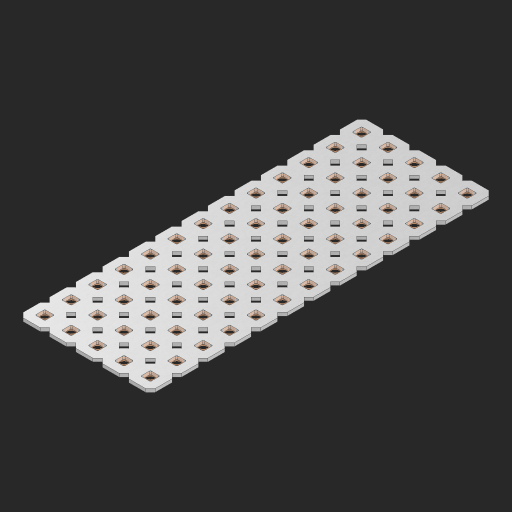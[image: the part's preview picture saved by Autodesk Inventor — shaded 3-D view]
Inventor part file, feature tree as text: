
AUTODESK INVENTOR PART (.ipt)
format: ipt  version: 2023 (Build 270158000, 158)  size: 1,042,432 bytes
history: native  units: in
note: dims shown in document units (in); Inventor stores cm internally (conversion verified against a paired STEP export)
features: other x66, extrude x64, sketch x2, pattern_linear x1
ambient origin geometry x8: Origin, YZ Plane, XZ Plane, XY Plane, X Axis, Y Axis, Z Axis, Center Point
bodies: Solid1 (feature_tree), Body (feature_tree)
feature tree (133):
  pattern_linear  "Rectangular Pattern1"  Spacing1=0.09in  [1 undecoded]
  sketch  "Sketch1"  dims[d1=0.5in]
  sketch  "Sketch2"  dims[d2=0.182in d3=0.09in d4=0.09in d5=0.09in d6=0.09in d7=0.09in d8=0.09in d9=0.09in d10=0.09in d11=0.02in d13=0.0in d14=0.172in d15=0.0625in d16=0.0in d19=0.5in d22=0.5in]
  other  "Srf1"
  other  "Srf126"
  other  "Srf127"
  other  "Srf128"
  other  "Srf129"
  other  "Srf130"
  other  "Srf131"
  other  "Srf250"
  other  "Srf251"
  other  "Srf252"
  other  "Srf253"
  other  "Srf254"
  other  "Srf255"
  other  "Srf268"
  other  "Srf269"
  other  "Srf270"
  other  "Srf271"
  other  "Srf272"
  other  "Srf273"
  other  "Srf274"
  other  "Srf275"
  other  "Srf276"
  other  "Srf277"
  other  "Srf278"
  other  "Srf279"
  other  "Srf280"
  other  "Srf293"
  other  "Srf294"
  other  "Srf295"
  other  "Srf296"
  other  "Srf297"
  other  "Srf298"
  other  "Srf299"
  other  "Srf300"
  other  "Srf301"
  other  "Srf302"
  other  "Srf303"
  other  "Srf304"
  other  "Srf305"
  other  "Srf318"
  other  "Srf319"
  other  "Srf320"
  other  "Srf321"
  other  "Srf322"
  other  "Srf323"
  other  "Srf324"
  other  "Srf325"
  other  "Srf326"
  other  "Srf327"
  other  "Srf328"
  other  "Srf329"
  other  "Srf330"
  other  "Srf343"
  other  "Srf344"
  other  "Srf345"
  other  "Srf346"
  other  "Srf347"
  other  "Srf348"
  other  "Srf349"
  other  "Srf350"
  other  "Srf351"
  other  "Srf352"
  other  "Srf353"
  other  "Srf354"
  other  "Srf355"
  other  "Circle"
  extrude  "ExtrusionSrf126"  Depth=0.09in
  extrude  "ExtrusionSrf127"  Depth=0.09in
  extrude  "ExtrusionSrf128"  Depth=0.09in
  extrude  "ExtrusionSrf129"  Depth=0.09in
  extrude  "ExtrusionSrf130"  Depth=0.09in
  extrude  "ExtrusionSrf131"  Depth=0.09in
  extrude  "ExtrusionSrf250"  Depth=0.09in
  extrude  "ExtrusionSrf251"  Depth=0.02in
  extrude  "ExtrusionSrf252"  TaperAngle=0.0deg  [1 undecoded]
  extrude  "ExtrusionSrf253"  Depth=0.5in
  extrude  "ExtrusionSrf254"  Depth=0.0625in TaperAngle=0.0deg
  extrude  "ExtrusionSrf255"  Depth=0.5in
  extrude  "ExtrusionSrf268"  Depth=0.5in
  extrude  "ExtrusionSrf269"  [1 undecoded]
  extrude  "ExtrusionSrf270"  [1 undecoded]
  extrude  "ExtrusionSrf271"  [1 undecoded]
  extrude  "ExtrusionSrf272"  [1 undecoded]
  extrude  "ExtrusionSrf273"  [1 undecoded]
  extrude  "ExtrusionSrf274"  [1 undecoded]
  extrude  "ExtrusionSrf275"  [1 undecoded]
  extrude  "ExtrusionSrf276"  [1 undecoded]
  extrude  "ExtrusionSrf277"  [1 undecoded]
  extrude  "ExtrusionSrf278"  [1 undecoded]
  extrude  "ExtrusionSrf279"  [1 undecoded]
  extrude  "ExtrusionSrf280"  [1 undecoded]
  extrude  "ExtrusionSrf293"  [1 undecoded]
  extrude  "ExtrusionSrf294"  [1 undecoded]
  extrude  "ExtrusionSrf295"  [1 undecoded]
  extrude  "ExtrusionSrf296"  [1 undecoded]
  extrude  "ExtrusionSrf297"  [1 undecoded]
  extrude  "ExtrusionSrf298"  [1 undecoded]
  extrude  "ExtrusionSrf299"  [1 undecoded]
  extrude  "ExtrusionSrf300"  [1 undecoded]
  extrude  "ExtrusionSrf301"  [1 undecoded]
  extrude  "ExtrusionSrf302"  [1 undecoded]
  extrude  "ExtrusionSrf303"  [1 undecoded]
  extrude  "ExtrusionSrf304"  [1 undecoded]
  extrude  "ExtrusionSrf305"  [1 undecoded]
  extrude  "ExtrusionSrf318"  [1 undecoded]
  extrude  "ExtrusionSrf319"  [1 undecoded]
  extrude  "ExtrusionSrf320"  [1 undecoded]
  extrude  "ExtrusionSrf321"  [1 undecoded]
  extrude  "ExtrusionSrf322"  [1 undecoded]
  extrude  "ExtrusionSrf323"  [1 undecoded]
  extrude  "ExtrusionSrf324"  [1 undecoded]
  extrude  "ExtrusionSrf325"  [1 undecoded]
  extrude  "ExtrusionSrf326"  [1 undecoded]
  extrude  "ExtrusionSrf327"  [1 undecoded]
  extrude  "ExtrusionSrf328"  [1 undecoded]
  extrude  "ExtrusionSrf329"  [1 undecoded]
  extrude  "ExtrusionSrf330"  [1 undecoded]
  extrude  "ExtrusionSrf343"  [1 undecoded]
  extrude  "ExtrusionSrf344"  [1 undecoded]
  extrude  "ExtrusionSrf345"  [1 undecoded]
  extrude  "ExtrusionSrf346"  [1 undecoded]
  extrude  "ExtrusionSrf347"  [1 undecoded]
  extrude  "ExtrusionSrf348"  [1 undecoded]
  extrude  "ExtrusionSrf349"  [1 undecoded]
  extrude  "ExtrusionSrf350"  [1 undecoded]
  extrude  "ExtrusionSrf351"  [1 undecoded]
  extrude  "ExtrusionSrf352"  [1 undecoded]
  extrude  "ExtrusionSrf353"  [1 undecoded]
  extrude  "ExtrusionSrf354"  [1 undecoded]
  extrude  "ExtrusionSrf355"  [1 undecoded]
note: 53 required parameter values undecoded (feature->parameter linkage not recoverable at this tier; creation-order binding heuristic only, values carry confidence <= 0.55)
